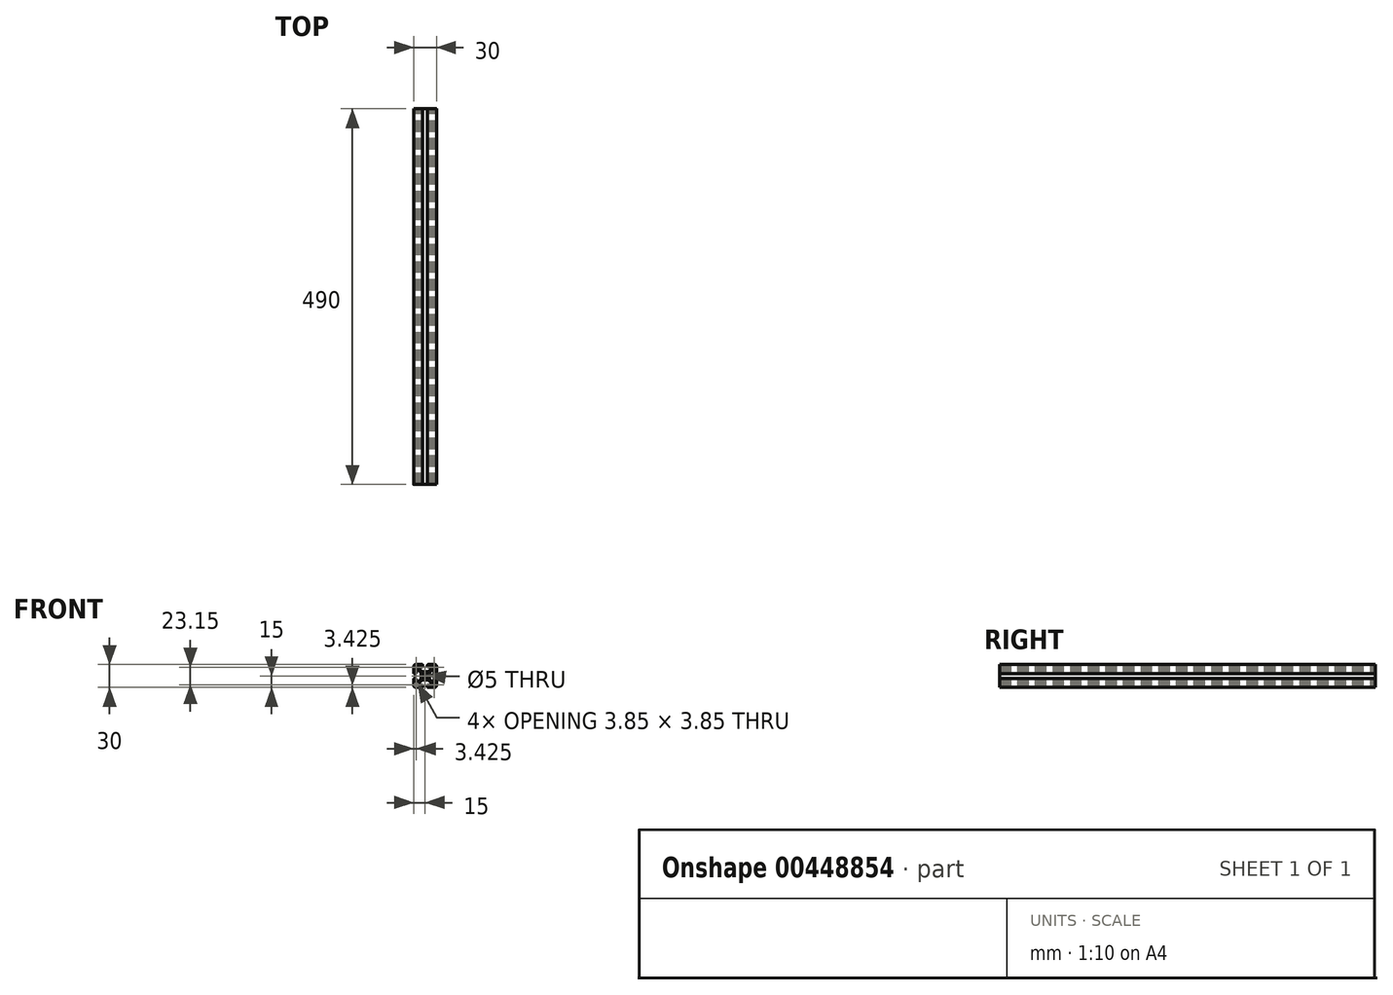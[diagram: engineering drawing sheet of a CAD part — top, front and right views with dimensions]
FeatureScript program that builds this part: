
annotation { "Feature Type Name" : "Feature", "Feature Type Description" : "" }
export const myFeature = defineFeature(function(context is Context, id is Id, definition is map)
    precondition{}
    {
        {
            var Q0;
            Q0=qCreatedBy(makeId("Front.planeOp"),FACE);
            var sketch = newSketch(context, id + "F0", { "sketchPlane" : qUnion([Q0])});
            skLineSegment(sketch, "E0", {"start": v(0, 5.25) * mm, "end": v(2.6, 5.25) * mm});
            skLineSegment(sketch, "E1", {"start": v(4.71, 6.13) * mm, "end": v(7.27, 8.69) * mm});
            skLineSegment(sketch, "E2", {"start": v(8.15, 10.8) * mm, "end": v(8.15, 12.5) * mm});
            skLineSegment(sketch, "E3", {"start": v(7.15, 13.5) * mm, "end": v(5.9, 13.5) * mm});
            skLineSegment(sketch, "E4", {"start": v(5.6, 13.2) * mm, "end": v(5.6, 12.3) * mm});
            skLineSegment(sketch, "E5", {"start": v(5.3, 12) * mm, "end": v(3.9, 12) * mm});
            skLineSegment(sketch, "E6", {"start": v(3.1, 12.8) * mm, "end": v(3.1, 14) * mm});
            skLineSegment(sketch, "E7", {"start": v(4.1, 15) * mm, "end": v(12, 15) * mm});
            skPoint(sketch, "E8.visualSharp", {"position": v(3.84, 5.25) * mm});
            skArc(sketch, "E8.filletArc", {"start": v(2.6, 5.25) * mm, "mid": v(3.74, 5.48) * mm, "end": v(4.71, 6.13) * mm});
            skPoint(sketch, "E9.visualSharp", {"position": v(8.15, 9.56) * mm});
            skArc(sketch, "E9.filletArc", {"start": v(7.27, 8.69) * mm, "mid": v(7.92, 9.66) * mm, "end": v(8.15, 10.8) * mm});
            skPoint(sketch, "E10.visualSharp", {"position": v(8.15, 13.5) * mm});
            skArc(sketch, "E10.filletArc", {"start": v(8.15, 12.5) * mm, "mid": v(7.86, 13.2) * mm, "end": v(7.15, 13.5) * mm});
            skPoint(sketch, "E11.visualSharp", {"position": v(5.6, 13.5) * mm});
            skArc(sketch, "E11.filletArc", {"start": v(5.9, 13.5) * mm, "mid": v(5.69, 13.41) * mm, "end": v(5.6, 13.2) * mm});
            skPoint(sketch, "E12.visualSharp", {"position": v(5.6, 12) * mm});
            skArc(sketch, "E12.filletArc", {"start": v(5.3, 12) * mm, "mid": v(5.51, 12.09) * mm, "end": v(5.6, 12.3) * mm});
            skPoint(sketch, "E13.visualSharp", {"position": v(3.1, 12) * mm});
            skArc(sketch, "E13.filletArc", {"start": v(3.1, 12.8) * mm, "mid": v(3.33, 12.23) * mm, "end": v(3.9, 12) * mm});
            skPoint(sketch, "E14.visualSharp", {"position": v(3.1, 15) * mm});
            skArc(sketch, "E14.filletArc", {"start": v(4.1, 15) * mm, "mid": v(3.4, 14.7) * mm, "end": v(3.1, 14) * mm});
            skArc(sketch, "E15.MirrorCS", {"start": v(12, 5.3) * mm, "mid": v(12.09, 5.51) * mm, "end": v(12.3, 5.6) * mm});
            skArc(sketch, "E16.MirrorCS", {"start": v(13.5, 5.9) * mm, "mid": v(13.41, 5.69) * mm, "end": v(13.2, 5.6) * mm});
            skPoint(sketch, "E17.MirrorP", {"position": v(13.5, 5.6) * mm});
            skLineSegment(sketch, "E18.MirrorCS", {"start": v(5.25, 0) * mm, "end": v(5.25, 2.6) * mm});
            skLineSegment(sketch, "E19.MirrorCS", {"start": v(6.13, 4.71) * mm, "end": v(8.69, 7.27) * mm});
            skPoint(sketch, "E20.MirrorP", {"position": v(13.5, 8.15) * mm});
            skLineSegment(sketch, "E21.MirrorCS", {"start": v(10.8, 8.15) * mm, "end": v(12.5, 8.15) * mm});
            skLineSegment(sketch, "E22.MirrorCS", {"start": v(13.5, 7.15) * mm, "end": v(13.5, 5.9) * mm});
            skPoint(sketch, "E23.MirrorP", {"position": v(9.56, 8.15) * mm});
            skLineSegment(sketch, "E24.MirrorCS", {"start": v(13.2, 5.6) * mm, "end": v(12.3, 5.6) * mm});
            skArc(sketch, "E25.MirrorCS", {"start": v(15, 4.1) * mm, "mid": v(14.7, 3.4) * mm, "end": v(14, 3.1) * mm});
            skArc(sketch, "E26.MirrorCS", {"start": v(12.8, 3.1) * mm, "mid": v(12.23, 3.33) * mm, "end": v(12, 3.9) * mm});
            skPoint(sketch, "E27.MirrorP", {"position": v(12, 5.6) * mm});
            skLineSegment(sketch, "E28.MirrorCS", {"start": v(12, 5.3) * mm, "end": v(12, 3.9) * mm});
            skPoint(sketch, "E29.MirrorP", {"position": v(5.25, 3.84) * mm});
            skLineSegment(sketch, "E30.MirrorCS", {"start": v(15, 4.1) * mm, "end": v(15, 12) * mm});
            skLineSegment(sketch, "E31.MirrorCS", {"start": v(12.8, 3.1) * mm, "end": v(14, 3.1) * mm});
            skArc(sketch, "E32.MirrorCS", {"start": v(5.25, 2.6) * mm, "mid": v(5.48, 3.74) * mm, "end": v(6.13, 4.71) * mm});
            skArc(sketch, "E33.MirrorCS", {"start": v(12.5, 8.15) * mm, "mid": v(13.2, 7.86) * mm, "end": v(13.5, 7.15) * mm});
            skArc(sketch, "E34.MirrorCS", {"start": v(8.69, 7.27) * mm, "mid": v(9.66, 7.92) * mm, "end": v(10.8, 8.15) * mm});
            skPoint(sketch, "E35.MirrorP", {"position": v(15, 3.1) * mm});
            skPoint(sketch, "E36.MirrorP", {"position": v(12, 3.1) * mm});
            skArc(sketch, "E37.MirrorCS", {"start": v(-5.9, 13.5) * mm, "mid": v(-5.69, 13.41) * mm, "end": v(-5.6, 13.2) * mm});
            skLineSegment(sketch, "E38.MirrorCS", {"start": v(-5.6, 13.2) * mm, "end": v(-5.6, 12.3) * mm});
            skArc(sketch, "E39.MirrorCS", {"start": v(-5.3, 12) * mm, "mid": v(-5.51, 12.09) * mm, "end": v(-5.6, 12.3) * mm});
            skArc(sketch, "E40.MirrorCS", {"start": v(-12, 5.3) * mm, "mid": v(-12.09, 5.51) * mm, "end": v(-12.3, 5.6) * mm});
            skLineSegment(sketch, "E41.MirrorCS", {"start": v(-13.2, 5.6) * mm, "end": v(-12.3, 5.6) * mm});
            skArc(sketch, "E42.MirrorCS", {"start": v(-13.5, 5.9) * mm, "mid": v(-13.41, 5.69) * mm, "end": v(-13.2, 5.6) * mm});
            skArc(sketch, "E43.MirrorCS", {"start": v(-12.5, 8.15) * mm, "mid": v(-13.2, 7.86) * mm, "end": v(-13.5, 7.15) * mm});
            skArc(sketch, "E44.MirrorCS", {"start": v(-15, 4.1) * mm, "mid": v(-14.7, 3.4) * mm, "end": v(-14, 3.1) * mm});
            skArc(sketch, "E45.MirrorCS", {"start": v(-8.15, 12.5) * mm, "mid": v(-7.86, 13.2) * mm, "end": v(-7.15, 13.5) * mm});
            skLineSegment(sketch, "E46.MirrorCS", {"start": v(-5.3, 12) * mm, "end": v(-3.9, 12) * mm});
            skLineSegment(sketch, "E47.MirrorCS", {"start": v(-7.15, 13.5) * mm, "end": v(-5.9, 13.5) * mm});
            skArc(sketch, "E48.MirrorCS", {"start": v(-3.1, 12.8) * mm, "mid": v(-3.33, 12.23) * mm, "end": v(-3.9, 12) * mm});
            skArc(sketch, "E49.MirrorCS", {"start": v(-4.1, 15) * mm, "mid": v(-3.4, 14.7) * mm, "end": v(-3.1, 14) * mm});
            skArc(sketch, "E50.MirrorCS", {"start": v(-12.8, 3.1) * mm, "mid": v(-12.23, 3.33) * mm, "end": v(-12, 3.9) * mm});
            skPoint(sketch, "E51.MirrorP", {"position": v(-12, 3.1) * mm});
            skLineSegment(sketch, "E52.MirrorCS", {"start": v(-5.25, 0) * mm, "end": v(-5.25, 2.6) * mm});
            skLineSegment(sketch, "E53.MirrorCS", {"start": v(-10.8, 8.15) * mm, "end": v(-12.5, 8.15) * mm});
            skPoint(sketch, "E54.MirrorP", {"position": v(-9.56, 8.15) * mm});
            skLineSegment(sketch, "E55.MirrorCS", {"start": v(-12, 5.3) * mm, "end": v(-12, 3.9) * mm});
            skLineSegment(sketch, "E56.MirrorCS", {"start": v(-12.8, 3.1) * mm, "end": v(-14, 3.1) * mm});
            skArc(sketch, "E57.MirrorCS", {"start": v(-7.27, 8.69) * mm, "mid": v(-7.92, 9.66) * mm, "end": v(-8.15, 10.8) * mm});
            skArc(sketch, "E58.MirrorCS", {"start": v(-2.6, 5.25) * mm, "mid": v(-3.74, 5.48) * mm, "end": v(-4.71, 6.13) * mm});
            skLineSegment(sketch, "E59.MirrorCS", {"start": v(-4.1, 15) * mm, "end": v(-12, 15) * mm});
            skLineSegment(sketch, "E60.MirrorCS", {"start": v(-3.1, 12.8) * mm, "end": v(-3.1, 14) * mm});
            skPoint(sketch, "E61.MirrorP", {"position": v(-8.15, 9.56) * mm});
            skPoint(sketch, "E62.MirrorP", {"position": v(-8.15, 13.5) * mm});
            skPoint(sketch, "E63.MirrorP", {"position": v(-5.25, 3.84) * mm});
            skLineSegment(sketch, "E64.MirrorCS", {"start": v(-8.15, 10.8) * mm, "end": v(-8.15, 12.5) * mm});
            skPoint(sketch, "E65.MirrorP", {"position": v(-15, 3.1) * mm});
            skPoint(sketch, "E66.MirrorP", {"position": v(-5.6, 13.5) * mm});
            skPoint(sketch, "E67.MirrorP", {"position": v(-3.1, 15) * mm});
            skLineSegment(sketch, "E68.MirrorCS", {"start": v(-6.13, 4.71) * mm, "end": v(-8.69, 7.27) * mm});
            skLineSegment(sketch, "E69.MirrorCS", {"start": v(-4.71, 6.13) * mm, "end": v(-7.27, 8.69) * mm});
            skArc(sketch, "E70.MirrorCS", {"start": v(-8.69, 7.27) * mm, "mid": v(-9.66, 7.92) * mm, "end": v(-10.8, 8.15) * mm});
            skLineSegment(sketch, "E71.MirrorCS", {"start": v(-13.5, 7.15) * mm, "end": v(-13.5, 5.9) * mm});
            skPoint(sketch, "E72.MirrorP", {"position": v(-13.5, 8.15) * mm});
            skPoint(sketch, "E73.MirrorP", {"position": v(-3.1, 12) * mm});
            skPoint(sketch, "E74.MirrorP", {"position": v(-3.84, 5.25) * mm});
            skPoint(sketch, "E75.MirrorP", {"position": v(-5.6, 12) * mm});
            skLineSegment(sketch, "E76.MirrorCS", {"start": v(0, 5.25) * mm, "end": v(-2.6, 5.25) * mm});
            skLineSegment(sketch, "E77.MirrorCS", {"start": v(-15, 4.1) * mm, "end": v(-15, 12) * mm});
            skArc(sketch, "E78.MirrorCS", {"start": v(-5.25, 2.6) * mm, "mid": v(-5.48, 3.74) * mm, "end": v(-6.13, 4.71) * mm});
            skPoint(sketch, "E79.MirrorP", {"position": v(-12, 5.6) * mm});
            skPoint(sketch, "E80.MirrorP", {"position": v(-13.5, 5.6) * mm});
            skLineSegment(sketch, "E81.MirrorCS", {"start": v(5.6, -13.2) * mm, "end": v(5.6, -12.3) * mm});
            skArc(sketch, "E82.MirrorCS", {"start": v(5.9, -13.5) * mm, "mid": v(5.69, -13.41) * mm, "end": v(5.6, -13.2) * mm});
            skArc(sketch, "E83.MirrorCS", {"start": v(5.3, -12) * mm, "mid": v(5.51, -12.09) * mm, "end": v(5.6, -12.3) * mm});
            skArc(sketch, "E84.MirrorCS", {"start": v(-12, -5.3) * mm, "mid": v(-12.09, -5.51) * mm, "end": v(-12.3, -5.6) * mm});
            skArc(sketch, "E85.MirrorCS", {"start": v(-5.9, -13.5) * mm, "mid": v(-5.69, -13.41) * mm, "end": v(-5.6, -13.2) * mm});
            skLineSegment(sketch, "E86.MirrorCS", {"start": v(13.2, -5.6) * mm, "end": v(12.3, -5.6) * mm});
            skArc(sketch, "E87.MirrorCS", {"start": v(-5.3, -12) * mm, "mid": v(-5.51, -12.09) * mm, "end": v(-5.6, -12.3) * mm});
            skArc(sketch, "E88.MirrorCS", {"start": v(13.5, -5.9) * mm, "mid": v(13.41, -5.69) * mm, "end": v(13.2, -5.6) * mm});
            skLineSegment(sketch, "E89.MirrorCS", {"start": v(-5.6, -13.2) * mm, "end": v(-5.6, -12.3) * mm});
            skArc(sketch, "E90.MirrorCS", {"start": v(-13.5, -5.9) * mm, "mid": v(-13.41, -5.69) * mm, "end": v(-13.2, -5.6) * mm});
            skArc(sketch, "E91.MirrorCS", {"start": v(12, -5.3) * mm, "mid": v(12.09, -5.51) * mm, "end": v(12.3, -5.6) * mm});
            skLineSegment(sketch, "E92.MirrorCS", {"start": v(-13.2, -5.6) * mm, "end": v(-12.3, -5.6) * mm});
            skArc(sketch, "E93.MirrorCS", {"start": v(-15, -4.1) * mm, "mid": v(-14.7, -3.4) * mm, "end": v(-14, -3.1) * mm});
            skArc(sketch, "E94.MirrorCS", {"start": v(-12.5, -8.15) * mm, "mid": v(-13.2, -7.86) * mm, "end": v(-13.5, -7.15) * mm});
            skArc(sketch, "E95.MirrorCS", {"start": v(12.8, -3.1) * mm, "mid": v(12.23, -3.33) * mm, "end": v(12, -3.9) * mm});
            skArc(sketch, "E96.MirrorCS", {"start": v(-12.8, -3.1) * mm, "mid": v(-12.23, -3.33) * mm, "end": v(-12, -3.9) * mm});
            skLineSegment(sketch, "E97.MirrorCS", {"start": v(7.15, -13.5) * mm, "end": v(5.9, -13.5) * mm});
            skLineSegment(sketch, "E98.MirrorCS", {"start": v(5.3, -12) * mm, "end": v(3.9, -12) * mm});
            skArc(sketch, "E99.MirrorCS", {"start": v(8.15, -12.5) * mm, "mid": v(7.86, -13.2) * mm, "end": v(7.15, -13.5) * mm});
            skArc(sketch, "E100.MirrorCS", {"start": v(-4.1, -15) * mm, "mid": v(-3.4, -14.7) * mm, "end": v(-3.1, -14) * mm});
            skArc(sketch, "E101.MirrorCS", {"start": v(-3.1, -12.8) * mm, "mid": v(-3.33, -12.23) * mm, "end": v(-3.9, -12) * mm});
            skArc(sketch, "E102.MirrorCS", {"start": v(15, -4.1) * mm, "mid": v(14.7, -3.4) * mm, "end": v(14, -3.1) * mm});
            skArc(sketch, "E103.MirrorCS", {"start": v(-8.15, -12.5) * mm, "mid": v(-7.86, -13.2) * mm, "end": v(-7.15, -13.5) * mm});
            skArc(sketch, "E104.MirrorCS", {"start": v(12.5, -8.15) * mm, "mid": v(13.2, -7.86) * mm, "end": v(13.5, -7.15) * mm});
            skArc(sketch, "E105.MirrorCS", {"start": v(3.1, -12.8) * mm, "mid": v(3.33, -12.23) * mm, "end": v(3.9, -12) * mm});
            skArc(sketch, "E106.MirrorCS", {"start": v(4.1, -15) * mm, "mid": v(3.4, -14.7) * mm, "end": v(3.1, -14) * mm});
            skPoint(sketch, "E107.MirrorP", {"position": v(-3.1, -15) * mm});
            skArc(sketch, "E108.MirrorCS", {"start": v(-2.6, -5.25) * mm, "mid": v(-3.74, -5.48) * mm, "end": v(-4.71, -6.13) * mm});
            skLineSegment(sketch, "E109.MirrorCS", {"start": v(5.25, 0) * mm, "end": v(5.25, -2.6) * mm});
            skLineSegment(sketch, "E110.MirrorCS", {"start": v(-6.13, -4.71) * mm, "end": v(-8.69, -7.27) * mm});
            skLineSegment(sketch, "E111.MirrorCS", {"start": v(-12, -5.3) * mm, "end": v(-12, -3.9) * mm});
            skLineSegment(sketch, "E112.MirrorCS", {"start": v(12, -5.3) * mm, "end": v(12, -3.9) * mm});
            skLineSegment(sketch, "E113.MirrorCS", {"start": v(-7.15, -13.5) * mm, "end": v(-5.9, -13.5) * mm});
            skLineSegment(sketch, "E114.MirrorCS", {"start": v(-13.5, -7.15) * mm, "end": v(-13.5, -5.9) * mm});
            skPoint(sketch, "E115.MirrorP", {"position": v(5.6, -12) * mm});
            skPoint(sketch, "E116.MirrorP", {"position": v(12, -5.6) * mm});
            skPoint(sketch, "E117.MirrorP", {"position": v(-5.25, -3.84) * mm});
            skPoint(sketch, "E118.MirrorP", {"position": v(3.1, -15) * mm});
            skPoint(sketch, "E119.MirrorP", {"position": v(-5.6, -13.5) * mm});
            skArc(sketch, "E120.MirrorCS", {"start": v(-7.27, -8.69) * mm, "mid": v(-7.92, -9.66) * mm, "end": v(-8.15, -10.8) * mm});
            skPoint(sketch, "E121.MirrorP", {"position": v(8.15, -9.56) * mm});
            skPoint(sketch, "E122.MirrorP", {"position": v(9.56, -8.15) * mm});
            skPoint(sketch, "E123.MirrorP", {"position": v(-3.1, -12) * mm});
            skArc(sketch, "E124.MirrorCS", {"start": v(8.69, -7.27) * mm, "mid": v(9.66, -7.92) * mm, "end": v(10.8, -8.15) * mm});
            skLineSegment(sketch, "E125.MirrorCS", {"start": v(-8.15, -10.8) * mm, "end": v(-8.15, -12.5) * mm});
            skLineSegment(sketch, "E126.MirrorCS", {"start": v(-10.8, -8.15) * mm, "end": v(-12.5, -8.15) * mm});
            skLineSegment(sketch, "E127.MirrorCS", {"start": v(13.5, -7.15) * mm, "end": v(13.5, -5.9) * mm});
            skPoint(sketch, "E128.MirrorP", {"position": v(-9.56, -8.15) * mm});
            skPoint(sketch, "E129.MirrorP", {"position": v(-13.5, -5.6) * mm});
            skLineSegment(sketch, "E130.MirrorCS", {"start": v(-5.3, -12) * mm, "end": v(-3.9, -12) * mm});
            skArc(sketch, "E131.MirrorCS", {"start": v(-8.69, -7.27) * mm, "mid": v(-9.66, -7.92) * mm, "end": v(-10.8, -8.15) * mm});
            skArc(sketch, "E132.MirrorCS", {"start": v(5.25, -2.6) * mm, "mid": v(5.48, -3.74) * mm, "end": v(6.13, -4.71) * mm});
            skArc(sketch, "E133.MirrorCS", {"start": v(-5.25, -2.6) * mm, "mid": v(-5.48, -3.74) * mm, "end": v(-6.13, -4.71) * mm});
            skPoint(sketch, "E134.MirrorP", {"position": v(12, -3.1) * mm});
            skPoint(sketch, "E135.MirrorP", {"position": v(-8.15, -13.5) * mm});
            skPoint(sketch, "E136.MirrorP", {"position": v(-5.6, -12) * mm});
            skPoint(sketch, "E137.MirrorP", {"position": v(8.15, -13.5) * mm});
            skPoint(sketch, "E138.MirrorP", {"position": v(-3.84, -5.25) * mm});
            skPoint(sketch, "E139.MirrorP", {"position": v(-8.15, -9.56) * mm});
            skPoint(sketch, "E140.MirrorP", {"position": v(15, -3.1) * mm});
            skLineSegment(sketch, "E141.MirrorCS", {"start": v(3.1, -12.8) * mm, "end": v(3.1, -14) * mm});
            skLineSegment(sketch, "E142.MirrorCS", {"start": v(4.1, -15) * mm, "end": v(12, -15) * mm});
            skArc(sketch, "E143.MirrorCS", {"start": v(2.6, -5.25) * mm, "mid": v(3.74, -5.48) * mm, "end": v(4.71, -6.13) * mm});
            skArc(sketch, "E144.MirrorCS", {"start": v(7.27, -8.69) * mm, "mid": v(7.92, -9.66) * mm, "end": v(8.15, -10.8) * mm});
            skPoint(sketch, "E145.MirrorP", {"position": v(-15, -3.1) * mm});
            skLineSegment(sketch, "E146.MirrorCS", {"start": v(-15, -4.1) * mm, "end": v(-15, -12) * mm});
            skLineSegment(sketch, "E147.MirrorCS", {"start": v(0, -5.25) * mm, "end": v(-2.6, -5.25) * mm});
            skLineSegment(sketch, "E148.MirrorCS", {"start": v(15, -4.1) * mm, "end": v(15, -12) * mm});
            skLineSegment(sketch, "E149.MirrorCS", {"start": v(12.8, -3.1) * mm, "end": v(14, -3.1) * mm});
            skLineSegment(sketch, "E150.MirrorCS", {"start": v(-4.71, -6.13) * mm, "end": v(-7.27, -8.69) * mm});
            skPoint(sketch, "E151.MirrorP", {"position": v(5.6, -13.5) * mm});
            skPoint(sketch, "E152.MirrorP", {"position": v(-12, -5.6) * mm});
            skPoint(sketch, "E153.MirrorP", {"position": v(5.25, -3.84) * mm});
            skPoint(sketch, "E154.MirrorP", {"position": v(-12, -3.1) * mm});
            skLineSegment(sketch, "E155.MirrorCS", {"start": v(10.8, -8.15) * mm, "end": v(12.5, -8.15) * mm});
            skPoint(sketch, "E156.MirrorP", {"position": v(3.84, -5.25) * mm});
            skPoint(sketch, "E157.MirrorP", {"position": v(13.5, -5.6) * mm});
            skPoint(sketch, "E158.MirrorP", {"position": v(-13.5, -8.15) * mm});
            skPoint(sketch, "E159.MirrorP", {"position": v(13.5, -8.15) * mm});
            skLineSegment(sketch, "E160.MirrorCS", {"start": v(0, -5.25) * mm, "end": v(2.6, -5.25) * mm});
            skLineSegment(sketch, "E161.MirrorCS", {"start": v(6.13, -4.71) * mm, "end": v(8.69, -7.27) * mm});
            skLineSegment(sketch, "E162.MirrorCS", {"start": v(-3.1, -12.8) * mm, "end": v(-3.1, -14) * mm});
            skLineSegment(sketch, "E163.MirrorCS", {"start": v(-5.25, 0) * mm, "end": v(-5.25, -2.6) * mm});
            skLineSegment(sketch, "E164.MirrorCS", {"start": v(-4.1, -15) * mm, "end": v(-12, -15) * mm});
            skLineSegment(sketch, "E165.MirrorCS", {"start": v(4.71, -6.13) * mm, "end": v(7.27, -8.69) * mm});
            skLineSegment(sketch, "E166.MirrorCS", {"start": v(-12.8, -3.1) * mm, "end": v(-14, -3.1) * mm});
            skLineSegment(sketch, "E167.MirrorCS", {"start": v(8.15, -10.8) * mm, "end": v(8.15, -12.5) * mm});
            skPoint(sketch, "E168.MirrorP", {"position": v(3.1, -12) * mm});
            skCircle(sketch, "E169", {"center": v(0, 0) * mm, "radius": 2.5 * mm});
            skLineSegment(sketch, "E170.bottom", {"start": v(9.95, 13.5) * mm, "end": v(12, 13.5) * mm});
            skLineSegment(sketch, "E170.top", {"start": v(9.95, 9.65) * mm, "end": v(13.2, 9.65) * mm});
            skLineSegment(sketch, "E170.left", {"start": v(9.65, 13.2) * mm, "end": v(9.65, 9.95) * mm});
            skLineSegment(sketch, "E170.right", {"start": v(13.5, 12) * mm, "end": v(13.5, 9.95) * mm});
            skPoint(sketch, "E171.visualSharp", {"position": v(9.65, 9.65) * mm});
            skArc(sketch, "E171.filletArc", {"start": v(9.65, 9.95) * mm, "mid": v(9.74, 9.74) * mm, "end": v(9.95, 9.65) * mm});
            skPoint(sketch, "E172.visualSharp", {"position": v(13.5, 9.65) * mm});
            skArc(sketch, "E172.filletArc", {"start": v(13.2, 9.65) * mm, "mid": v(13.41, 9.74) * mm, "end": v(13.5, 9.95) * mm});
            skPoint(sketch, "E173.visualSharp", {"position": v(9.65, 13.5) * mm});
            skArc(sketch, "E173.filletArc", {"start": v(9.95, 13.5) * mm, "mid": v(9.74, 13.41) * mm, "end": v(9.65, 13.2) * mm});
            skPoint(sketch, "E174.visualSharp", {"position": v(13.5, 13.5) * mm});
            skArc(sketch, "E174.filletArc", {"start": v(13.5, 12) * mm, "mid": v(13.06, 13.06) * mm, "end": v(12, 13.5) * mm});
            skArc(sketch, "E175.MirrorCS", {"start": v(-13.2, 9.65) * mm, "mid": v(-13.41, 9.74) * mm, "end": v(-13.5, 9.95) * mm});
            skArc(sketch, "E176.MirrorCS", {"start": v(-9.65, 9.95) * mm, "mid": v(-9.74, 9.74) * mm, "end": v(-9.95, 9.65) * mm});
            skArc(sketch, "E177.MirrorCS", {"start": v(-9.95, 13.5) * mm, "mid": v(-9.74, 13.41) * mm, "end": v(-9.65, 13.2) * mm});
            skPoint(sketch, "E178.MirrorP", {"position": v(-13.5, 9.65) * mm});
            skPoint(sketch, "E179.MirrorP", {"position": v(-9.65, 9.65) * mm});
            skArc(sketch, "E180.MirrorCS", {"start": v(-13.5, 12) * mm, "mid": v(-13.06, 13.06) * mm, "end": v(-12, 13.5) * mm});
            skLineSegment(sketch, "E181.MirrorCS", {"start": v(-13.5, 12) * mm, "end": v(-13.5, 9.95) * mm});
            skLineSegment(sketch, "E182.MirrorCS", {"start": v(-9.95, 13.5) * mm, "end": v(-12, 13.5) * mm});
            skPoint(sketch, "E183.MirrorP", {"position": v(-13.5, 13.5) * mm});
            skPoint(sketch, "E184.MirrorP", {"position": v(-9.65, 13.5) * mm});
            skLineSegment(sketch, "E185.MirrorCS", {"start": v(-9.95, 9.65) * mm, "end": v(-13.2, 9.65) * mm});
            skLineSegment(sketch, "E186.MirrorCS", {"start": v(-9.65, 13.2) * mm, "end": v(-9.65, 9.95) * mm});
            skArc(sketch, "E187.MirrorCS", {"start": v(-9.65, -9.95) * mm, "mid": v(-9.74, -9.74) * mm, "end": v(-9.95, -9.65) * mm});
            skArc(sketch, "E188.MirrorCS", {"start": v(-9.95, -13.5) * mm, "mid": v(-9.74, -13.41) * mm, "end": v(-9.65, -13.2) * mm});
            skArc(sketch, "E189.MirrorCS", {"start": v(-13.2, -9.65) * mm, "mid": v(-13.41, -9.74) * mm, "end": v(-13.5, -9.95) * mm});
            skArc(sketch, "E190.MirrorCS", {"start": v(-13.5, -12) * mm, "mid": v(-13.06, -13.06) * mm, "end": v(-12, -13.5) * mm});
            skLineSegment(sketch, "E191.MirrorCS", {"start": v(-13.5, -12) * mm, "end": v(-13.5, -9.95) * mm});
            skLineSegment(sketch, "E192.MirrorCS", {"start": v(-9.95, -13.5) * mm, "end": v(-12, -13.5) * mm});
            skLineSegment(sketch, "E193.MirrorCS", {"start": v(-9.95, -9.65) * mm, "end": v(-13.2, -9.65) * mm});
            skLineSegment(sketch, "E194.MirrorCS", {"start": v(-9.65, -13.2) * mm, "end": v(-9.65, -9.95) * mm});
            skPoint(sketch, "E195.MirrorP", {"position": v(-9.65, -13.5) * mm});
            skPoint(sketch, "E196.MirrorP", {"position": v(-13.5, -13.5) * mm});
            skPoint(sketch, "E197.MirrorP", {"position": v(-9.65, -9.65) * mm});
            skPoint(sketch, "E198.MirrorP", {"position": v(-13.5, -9.65) * mm});
            skArc(sketch, "E199.MirrorCS", {"start": v(9.95, -13.5) * mm, "mid": v(9.74, -13.41) * mm, "end": v(9.65, -13.2) * mm});
            skArc(sketch, "E200.MirrorCS", {"start": v(9.65, -9.95) * mm, "mid": v(9.74, -9.74) * mm, "end": v(9.95, -9.65) * mm});
            skArc(sketch, "E201.MirrorCS", {"start": v(13.2, -9.65) * mm, "mid": v(13.41, -9.74) * mm, "end": v(13.5, -9.95) * mm});
            skPoint(sketch, "E202.MirrorP", {"position": v(9.65, -13.5) * mm});
            skPoint(sketch, "E203.MirrorP", {"position": v(9.65, -9.65) * mm});
            skPoint(sketch, "E204.MirrorP", {"position": v(13.5, -9.65) * mm});
            skPoint(sketch, "E205.MirrorP", {"position": v(13.5, -13.5) * mm});
            skLineSegment(sketch, "E206.MirrorCS", {"start": v(9.95, -13.5) * mm, "end": v(12, -13.5) * mm});
            skLineSegment(sketch, "E207.MirrorCS", {"start": v(9.95, -9.65) * mm, "end": v(13.2, -9.65) * mm});
            skLineSegment(sketch, "E208.MirrorCS", {"start": v(13.5, -12) * mm, "end": v(13.5, -9.95) * mm});
            skLineSegment(sketch, "E209.MirrorCS", {"start": v(9.65, -13.2) * mm, "end": v(9.65, -9.95) * mm});
            skArc(sketch, "E210.MirrorCS", {"start": v(13.5, -12) * mm, "mid": v(13.06, -13.06) * mm, "end": v(12, -13.5) * mm});
            skPoint(sketch, "E211.visualSharp", {"position": v(15, 15) * mm});
            skArc(sketch, "E211.filletArc", {"start": v(15, 12) * mm, "mid": v(14.12, 14.12) * mm, "end": v(12, 15) * mm});
            skPoint(sketch, "E212.visualSharp", {"position": v(15, -15) * mm});
            skArc(sketch, "E212.filletArc", {"start": v(12, -15) * mm, "mid": v(14.12, -14.12) * mm, "end": v(15, -12) * mm});
            skPoint(sketch, "E213.visualSharp", {"position": v(-15, -15) * mm});
            skArc(sketch, "E213.filletArc", {"start": v(-15, -12) * mm, "mid": v(-14.12, -14.12) * mm, "end": v(-12, -15) * mm});
            skPoint(sketch, "E214.visualSharp", {"position": v(-15, 15) * mm});
            skArc(sketch, "E214.filletArc", {"start": v(-12, 15) * mm, "mid": v(-14.12, 14.12) * mm, "end": v(-15, 12) * mm});
            skSolve(sketch);
        }
        {
            var Q0;
            Q0=qSketchRegion(id+"F0",true);
            extrude(context, id + "F1", {"entities" : qUnion([Q0]), "depth" : 490 * mm});
        }
    });
